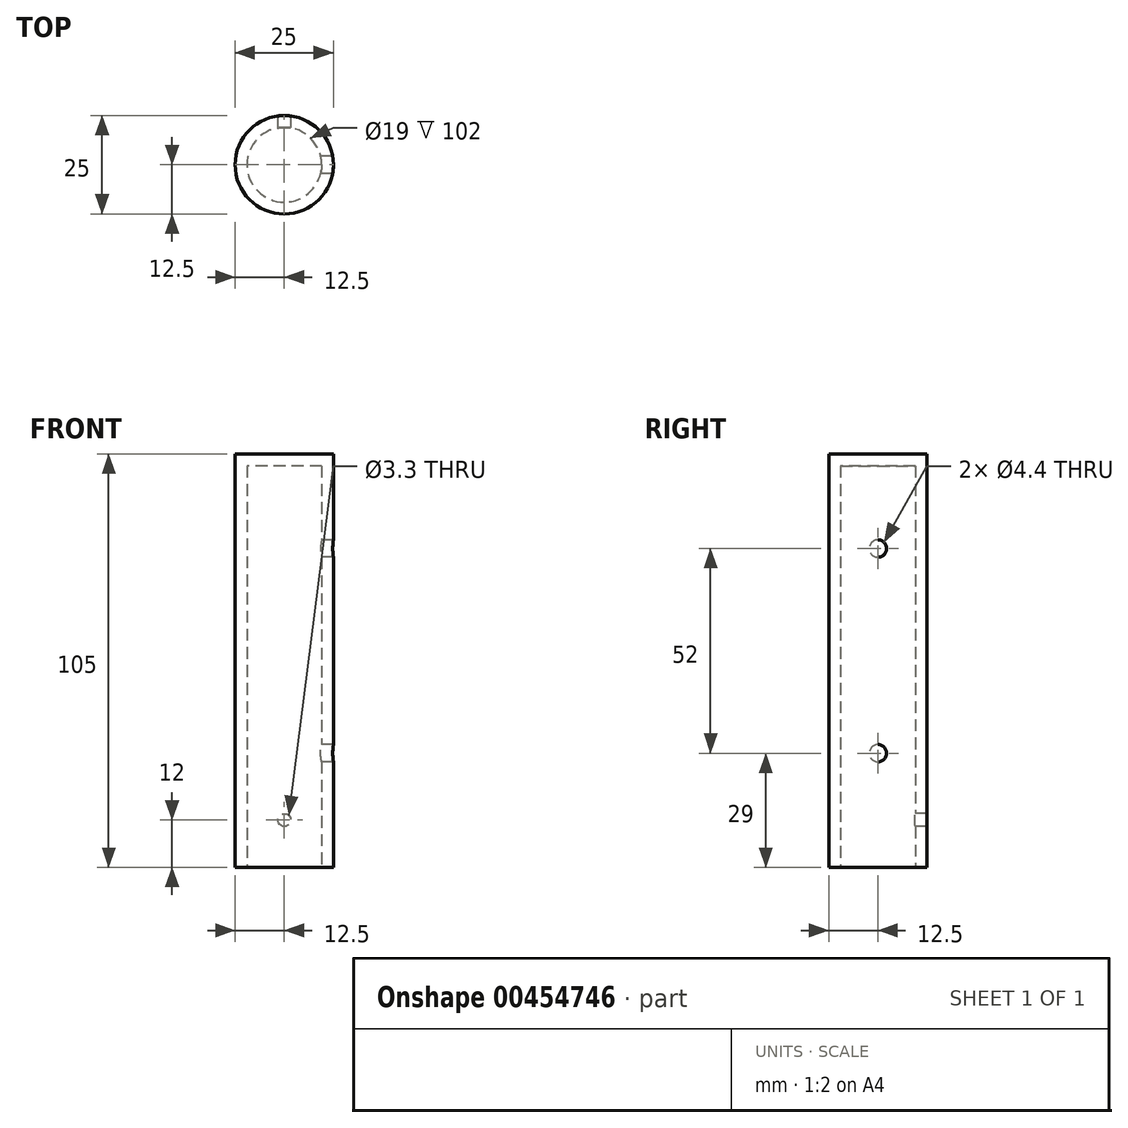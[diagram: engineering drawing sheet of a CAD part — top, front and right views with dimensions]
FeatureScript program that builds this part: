
annotation { "Feature Type Name" : "Feature", "Feature Type Description" : "" }
export const myFeature = defineFeature(function(context is Context, id is Id, definition is map)
    precondition{}
    {
        {
            var Q0;
            Q0=qCreatedBy(makeId("Top.planeOp"),FACE);
            var sketch = newSketch(context, id + "F0", { "sketchPlane" : qUnion([Q0])});
            skCircle(sketch, "E0", {"center": v(0, 0) * mm, "radius": 12.5 * mm});
            skCircle(sketch, "E1.0", {"center": v(0, 0) * mm, "radius": 9.5 * mm});
            skSolve(sketch);
        }
        {
            var Q0;
            Q0 = qSketchRegion(id + "F0", true);
            extrude(context, id + "F1", {"entities" : qUnion([Q0]), "depth" : 105 * mm});
        }
        {
            var Q0;
            Q0=makeQuery(id+"F1.opExtrude","CAP_FACE",FACE,{"disambiguationData":[OSD([sQuery(id+"F0.wireOp",EDGE,"E0"),sQuery(id+"F0.wireOp",EDGE,"E1.0")])],"isStart":false});
            var sketch = newSketch(context, id + "F2", { "sketchPlane" : qUnion([Q0])});
            skCircle(sketch, "E2.0", {"center": v(0, 0) * mm, "radius": 12.5 * mm});
            skSolve(sketch);
        }
        {
            var Q0;
            Q0 = qSketchRegion(id + "F2", true);
            extrude(context, id + "F3", {"entities" : qUnion([Q0]), "operationType" : NewBodyOperationType.ADD, "oppositeDirection" : true, "depth" : 3 * mm});
        }
        {
            var Q0;
            Q0=qCreatedBy(makeId("Front.planeOp"),FACE);
            var sketch = newSketch(context, id + "F4", { "sketchPlane" : qUnion([Q0])});
            skPoint(sketch, "E3", {"position": v(0, 12) * mm});
            skSolve(sketch);
        }
        {
            var Q0;
            Q0=sQuery(id+"F4.wireOp",VERTEX,"E3");
            var Q1;
            Q1=makeQuery(id+"F1.opExtrude","SWEPT_BODY",BODY,{"disambiguationData":[OSD([sQuery(id+"F0.wireOp",EDGE,"E0"),sQuery(id+"F0.wireOp",EDGE,"E1.0")])]});
            hole(context, id + "F5", {"style" : HoleStyle.SIMPLE, "endStyle" : HoleEndStyle.BLIND, "standardTappedOrClearance" : lookupTablePath({ "standard" : "ISO", "engagement" : "75%", "pitch" : "0.7 mm", "size" : "M4", "type" : "Tapped" }), "standardBlindInLast" : lookupTablePath({ "standard" : "ISO", "engagement" : "75%", "pitch" : "0.7 mm", "size" : "M4", "type" : "Tapped" }), "holeDiameter" : 3.3 * mm, "showTappedDepth" : true, "holeDepth" : 22.1 * mm, "isTappedThrough" : true, "tappedDepth" : 20 * mm, "tapClearance" : 3, "locations" : qUnion([Q0]), "scope" : qUnion([Q1]), "majorDiameter" : 4 * mm});
        }
        {
            var Q0;
            Q0=qCreatedBy(makeId("Right.planeOp"),FACE);
            var sketch = newSketch(context, id + "F6", { "sketchPlane" : qUnion([Q0])});
            skPoint(sketch, "E4", {"position": v(0, 81) * mm});
            skPoint(sketch, "E5", {"position": v(0, 29) * mm});
            skSolve(sketch);
        }
        {
            var Q0;
            Q0=sQuery(id+"F6.wireOp",VERTEX,"E4");
            var Q1;
            Q1=sQuery(id+"F6.wireOp",VERTEX,"E5");
            var Q2;
            Q2=makeQuery(id+"F1.opExtrude","SWEPT_BODY",BODY,{"disambiguationData":[OSD([sQuery(id+"F0.wireOp",EDGE,"E0"),sQuery(id+"F0.wireOp",EDGE,"E1.0")])]});
            hole(context, id + "F7", {"style" : HoleStyle.SIMPLE, "endStyle" : HoleEndStyle.BLIND, "oppositeDirection" : true, "standardTappedOrClearance" : lookupTablePath({ "standard" : "ISO", "fit" : "Normal", "size" : "M4", "type" : "Clearance" }), "standardBlindInLast" : lookupTablePath({ "fit" : "Standard", "standard" : "ISO", "size" : "M4", "type" : "Clearance" }), "holeDiameter" : 4.4 * mm, "holeDepth" : 22.1 * mm, "isTappedThrough" : true, "tappedDepth" : 20 * mm, "tapClearance" : 3, "locations" : qUnion([Q0, Q1]), "scope" : qUnion([Q2])});
        }
    });
